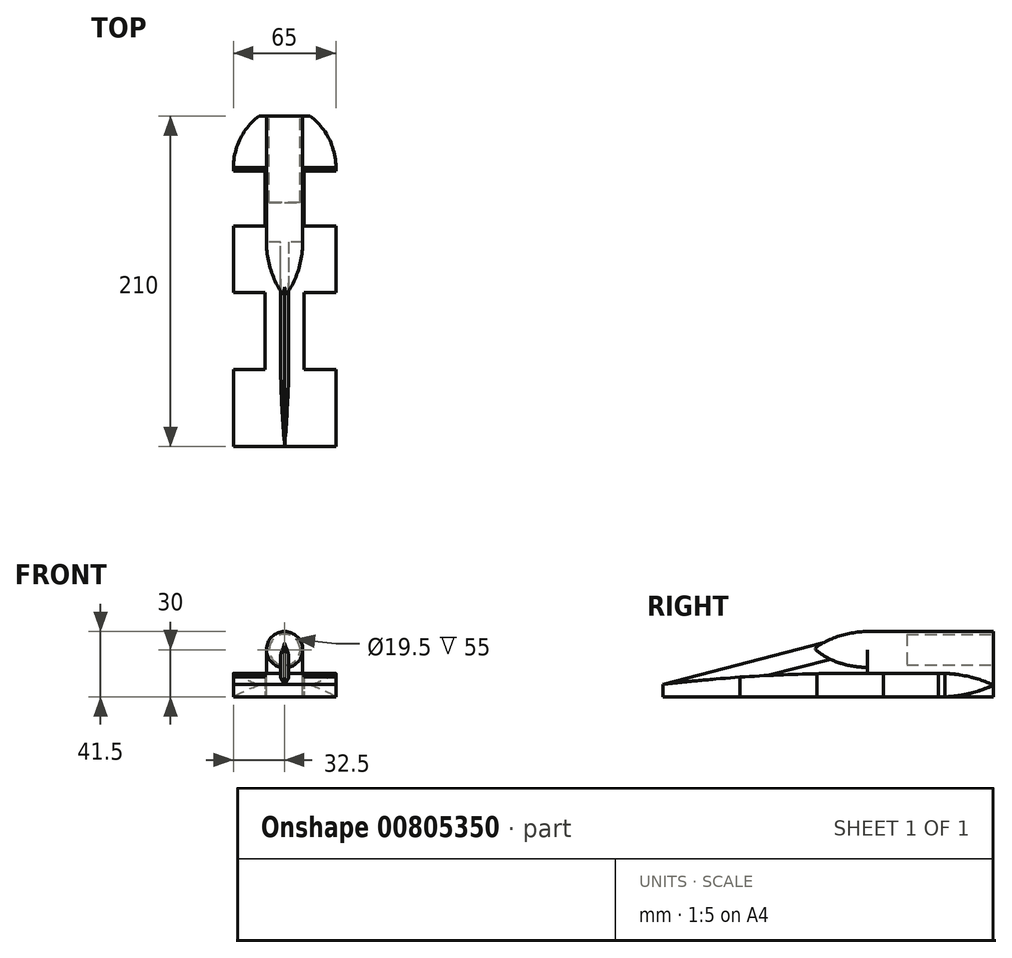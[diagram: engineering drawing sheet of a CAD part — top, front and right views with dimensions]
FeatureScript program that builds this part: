
annotation { "Feature Type Name" : "Feature", "Feature Type Description" : "" }
export const myFeature = defineFeature(function(context is Context, id is Id, definition is map)
    precondition{}
    {
        {
            var Q0;
            Q0=qCreatedBy(makeId("Right.planeOp"),FACE);
            var sketch = newSketch(context, id + "F0", { "sketchPlane" : qUnion([Q0])});
            skLineSegment(sketch, "E0", {"start": v(0, 0) * mm, "end": v(210, 0) * mm});
            skLineSegment(sketch, "E1", {"start": v(210, 0) * mm, "end": v(210, 15) * mm});
            skLineSegment(sketch, "E2", {"start": v(210, 15) * mm, "end": v(120, 15) * mm});
            skArc(sketch, "E3", {"start": v(120, 15) * mm, "mid": v(59.9, 13.25) * mm, "end": v(0, 8) * mm});
            skLineSegment(sketch, "E4", {"start": v(0, 8) * mm, "end": v(0, 0) * mm});
            skSolve(sketch);
        }
        {
            var Q0;
            Q0=makeQuery(id+"F0.imprint","IMPRINT",FACE,{"disambiguationData":[TD([[makeQuery(id+"F0.imprint","IMPRINT",EDGE,{"derivedFrom":sQuery(id+"F0.wireOp",EDGE,"E0")}),1.0]])]});
            extrude(context, id + "F1", {"entities" : qUnion([Q0]), "depth" : 32.5 * mm, "offsetDistance" : 25 * mm});
        }
        {
            var Q0;
            Q0=makeQuery(id+"F1.opExtrude","SWEPT_FACE",FACE,{"disambiguationData":[OSD([sQuery(id+"F0.wireOp",EDGE,"E0")])]});
            var sketch = newSketch(context, id + "F2", { "sketchPlane" : qUnion([Q0])});
            skLineSegment(sketch, "E5", {"start": v(32.5, -49) * mm, "end": v(12.5, -49) * mm});
            skLineSegment(sketch, "E6", {"start": v(12.5, -49) * mm, "end": v(12.5, -98) * mm});
            skLineSegment(sketch, "E7", {"start": v(12.5, -98) * mm, "end": v(32.5, -98) * mm});
            skLineSegment(sketch, "E8", {"start": v(32.5, -140) * mm, "end": v(12.5, -140) * mm});
            skLineSegment(sketch, "E9", {"start": v(12.5, -140) * mm, "end": v(12.5, -175) * mm});
            skLineSegment(sketch, "E10", {"start": v(12.5, -175) * mm, "end": v(32.5, -175) * mm});
            skArc(sketch, "E11", {"start": v(16.25, -210) * mm, "mid": v(28.72, -194.52) * mm, "end": v(32.5, -175) * mm});
            skSolve(sketch);
        }
        {
            var Q0;
            {var subQ0=sQuery(id+"F0.wireOp",EDGE,"E3");var subQ1=sQuery(id+"F0.wireOp",EDGE,"E2");var subQ2=sQuery(id+"F0.wireOp",EDGE,"E0");Q0=makeQuery(id+"F4.boolean.opBoolean","SPLIT",FACE,{"disambiguationData":[TD([makeQuery(id+"F4.opExtrude","SWEPT_FACE",FACE,{"disambiguationData":[OSD([sQuery(id+"F2.wireOp",EDGE,"E7")])]})])],"derivedFrom":makeQuery(id+"F1.opExtrude","CAP_FACE",FACE,{"disambiguationData":[OSD([subQ2,sQuery(id+"F0.wireOp",EDGE,"E1"),subQ1,subQ0,sQuery(id+"F0.wireOp",EDGE,"E4")])],"isStart":false})});}
            var sketch = newSketch(context, id + "F3", { "sketchPlane" : qUnion([Q0])});
            skLineSegment(sketch, "E12", {"start": v(175, 15) * mm, "end": v(175, 0) * mm});
            skArc(sketch, "E13", {"start": v(175, 0) * mm, "mid": v(192.92, 1.77) * mm, "end": v(210, 7.5) * mm});
            skArc(sketch, "E14", {"start": v(210, 7.5) * mm, "mid": v(192.92, 13.23) * mm, "end": v(175, 15) * mm});
            skSolve(sketch);
        }
        {
            var Q0;
            {var subQ0=sQuery(id+"F2.wireOp",EDGE,"E5");Q0=makeQuery(id+"F2.imprint","IMPRINT",FACE,{"disambiguationData":[TD([[makeQuery(id+"F2.imprint","IMPRINT",EDGE,{"derivedFrom":subQ0}),1.0]])]});}
            var Q1;
            {var subQ0=sQuery(id+"F2.wireOp",EDGE,"E8");Q1=makeQuery(id+"F2.imprint","IMPRINT",FACE,{"disambiguationData":[TD([[makeQuery(id+"F2.imprint","IMPRINT",EDGE,{"derivedFrom":subQ0}),1.0]])]});}
            var Q2;
            {var subQ0=sQuery(id+"F2.wireOp",EDGE,"E11");var subQ1=sQuery(id+"F0.wireOp",EDGE,"E0");var subQ4=makeQuery(id+"F1.opExtrude","CAP_EDGE",EDGE,{"disambiguationData":[OSD([subQ1])],"isStart":false});var subQ5=makeQuery(id+"F2.imprint","INTERSECT",VERTEX,{"derivedFrom":[subQ4,subQ0]});Q2=makeQuery(id+"F2.imprint","IMPRINT",FACE,{"disambiguationData":[TD([[makeQuery(id+"F2.imprint","IMPRINT",EDGE,{"disambiguationData":[TD([[subQ5,1.0]])],"derivedFrom":subQ0}),-1.0]])]});}
            extrude(context, id + "F4", {"entities" : qUnion([Q0, Q1, Q2]), "operationType" : NewBodyOperationType.REMOVE, "endBound" : BoundingType.THROUGH_ALL, "oppositeDirection" : true, "depth" : 25 * mm, "offsetDistance" : 25 * mm});
        }
        {
            var Q0;
            {var subQ1=makeQuery(id+"F1.opExtrude","CAP_EDGE",EDGE,{"disambiguationData":[OSD([sQuery(id+"F0.wireOp",EDGE,"E1")])],"isStart":false});var subQ3=makeQuery(id+"F1.opExtrude","CAP_EDGE",EDGE,{"disambiguationData":[OSD([sQuery(id+"F0.wireOp",EDGE,"E2")])],"isStart":false});var subQ5=makeQuery(id+"F3.imprint","INTERSECT",VERTEX,{"derivedFrom":[subQ1,subQ3]});Q0=makeQuery(id+"F3.imprint","IMPRINT",FACE,{"disambiguationData":[TD([[makeQuery(id+"F3.imprint","IMPRINT",EDGE,{"disambiguationData":[TD([[subQ5,-1.0]])],"derivedFrom":subQ3}),1.0]])]});}
            var Q1;
            {var subQ1=makeQuery(id+"F1.opExtrude","CAP_EDGE",EDGE,{"disambiguationData":[OSD([sQuery(id+"F0.wireOp",EDGE,"E1")])],"isStart":false});var subQ3=makeQuery(id+"F1.opExtrude","CAP_EDGE",EDGE,{"disambiguationData":[OSD([sQuery(id+"F0.wireOp",EDGE,"E0")])],"isStart":false});var subQ5=makeQuery(id+"F3.imprint","INTERSECT",VERTEX,{"derivedFrom":[subQ3,subQ1]});Q1=makeQuery(id+"F3.imprint","IMPRINT",FACE,{"disambiguationData":[TD([[makeQuery(id+"F3.imprint","IMPRINT",EDGE,{"disambiguationData":[TD([[subQ5,1.0]])],"derivedFrom":subQ3}),1.0]])]});}
            extrude(context, id + "F5", {"entities" : qUnion([Q0, Q1]), "operationType" : NewBodyOperationType.REMOVE, "oppositeDirection" : true, "depth" : 21 * mm, "offsetDistance" : 25 * mm});
        }
        {
            var Q0;
            Q0=makeQuery(id+"F1.opExtrude","SWEPT_BODY",BODY,{"disambiguationData":[OSD([sQuery(id+"F0.wireOp",EDGE,"E0"),sQuery(id+"F0.wireOp",EDGE,"E1"),sQuery(id+"F0.wireOp",EDGE,"E2"),sQuery(id+"F0.wireOp",EDGE,"E3"),sQuery(id+"F0.wireOp",EDGE,"E4")])]});
            var Q1;
            Q1=qCreatedBy(makeId("Right.planeOp"),FACE);
            mirror(context, id + "F6", {"operationType" : NewBodyOperationType.ADD, "entities" : qUnion([Q0]), "mirrorPlane" : qUnion([Q1])});
        }
        {
            var Q0;
            {var subQ0=makeQuery(id+"F1.opExtrude","SWEPT_FACE",FACE,{"disambiguationData":[OSD([sQuery(id+"F0.wireOp",EDGE,"E1")])]});Q0=makeQuery(id+"F6.boolean.opBoolean","MERGE",FACE,{"derivedFrom":[subQ0,makeQuery(id+"F6.opPattern","COPY",FACE,{"derivedFrom":subQ0,"instanceName":"1"})]});}
            var sketch = newSketch(context, id + "F7", { "sketchPlane" : qUnion([Q0])});
            skLineSegment(sketch, "E15", {"start": v(-11.5, 15) * mm, "end": v(-11.5, 30) * mm});
            skLineSegment(sketch, "E16", {"start": v(11.5, 15) * mm, "end": v(11.5, 30) * mm});
            skArc(sketch, "E17", {"start": v(11.5, 30) * mm, "mid": v(0, 41.5) * mm, "end": v(-11.5, 30) * mm});
            skCircle(sketch, "E18", {"center": v(0, 30) * mm, "radius": 9.75 * mm});
            skSolve(sketch);
        }
        {
            var Q0;
            Q0=makeQuery(id+"F7.imprint","IMPRINT",FACE,{"disambiguationData":[TD([[makeQuery(id+"F7.imprint","IMPRINT",EDGE,{"derivedFrom":sQuery(id+"F7.wireOp",EDGE,"E18")}),1.0]])]});
            var Q1;
            Q1=makeQuery(id+"F7.imprint","IMPRINT",FACE,{"disambiguationData":[TD([[makeQuery(id+"F7.imprint","IMPRINT",EDGE,{"derivedFrom":sQuery(id+"F7.wireOp",EDGE,"E15")}),-1.0]])]});
            extrude(context, id + "F8", {"entities" : qUnion([Q0, Q1]), "operationType" : NewBodyOperationType.ADD, "oppositeDirection" : true, "depth" : 80 * mm, "offsetDistance" : 25 * mm});
        }
        {
            var Q0;
            Q0=makeQuery(id+"F7.imprint","IMPRINT",FACE,{"disambiguationData":[TD([[makeQuery(id+"F7.imprint","IMPRINT",EDGE,{"derivedFrom":sQuery(id+"F7.wireOp",EDGE,"E18")}),1.0]])]});
            extrude(context, id + "F9", {"entities" : qUnion([Q0]), "operationType" : NewBodyOperationType.REMOVE, "oppositeDirection" : true, "depth" : 55 * mm, "offsetDistance" : 25 * mm});
        }
        {
            var Q0;
            Q0=qCreatedBy(makeId("Right.planeOp"),FACE);
            var sketch = newSketch(context, id + "F10", { "sketchPlane" : qUnion([Q0])});
            skLineSegment(sketch, "E19.0", {"start": v(130, 15) * mm, "end": v(130, 30) * mm});
            skLineSegment(sketch, "E20", {"start": v(130, 41.5) * mm, "end": v(210, 41.5) * mm});
            skLineSegment(sketch, "E21", {"start": v(130, 30) * mm, "end": v(95, 30) * mm});
            skArc(sketch, "E22", {"start": v(130, 41.5) * mm, "mid": v(111.58, 38.55) * mm, "end": v(95, 30) * mm});
            skLineSegment(sketch, "E23", {"start": v(130, 41.5) * mm, "end": v(130, 30) * mm});
            skSolve(sketch);
        }
        {
            var Q0;
            Q0 = qSketchRegion(id + "F10", true);
            var Q1;
            Q1=sQuery(id+"F10.wireOp",EDGE,"E21");
            revolve(context, id + "F11", {"surfaceOperationType" : NewSurfaceOperationType.NEW, "entities" : qUnion([Q0]), "axis" : qUnion([Q1]), "revolveType" : RevolveType.FULL});
        }
        {
            var Q0;
            Q0=makeQuery(id+"F8.opExtrude","CAP_FACE",FACE,{"disambiguationData":[OSD([sQuery(id+"F0.wireOp",EDGE,"E1"),sQuery(id+"F0.wireOp",EDGE,"E2"),sQuery(id+"F7.wireOp",EDGE,"E15"),sQuery(id+"F7.wireOp",EDGE,"E16"),sQuery(id+"F7.wireOp",EDGE,"E17")])],"isStart":false});
            var sketch = newSketch(context, id + "F12", { "sketchPlane" : qUnion([Q0])});
            skPoint(sketch, "E24.0", {"position": v(0, 15) * mm});
            skLineSegment(sketch, "E25.0", {"start": v(32.5, 15) * mm, "end": v(-32.5, 15) * mm});
            skArc(sketch, "E26", {"start": v(0, 41.5) * mm, "mid": v(-2.22, 35.96) * mm, "end": v(-2.5, 30) * mm});
            skArc(sketch, "E27", {"start": v(2.5, 30) * mm, "mid": v(2.22, 35.96) * mm, "end": v(0, 41.5) * mm});
            skLineSegment(sketch, "E28", {"start": v(2.5, 30) * mm, "end": v(2.5, 15) * mm});
            skLineSegment(sketch, "E29", {"start": v(-2.5, 30) * mm, "end": v(-2.5, 15) * mm});
            skLineSegment(sketch, "E30", {"start": v(-2.5, 15) * mm, "end": v(2.5, 15) * mm});
            skSolve(sketch);
        }
        {
            var Q0;
            Q0=qCreatedBy(makeId("Right.planeOp"),FACE);
            var sketch = newSketch(context, id + "F13", { "sketchPlane" : qUnion([Q0])});
            skPoint(sketch, "E31.0", {"position": v(130, 41.5) * mm});
            skPoint(sketch, "E32.0", {"position": v(0, 8) * mm});
            skLineSegment(sketch, "E33", {"start": v(130, 41.5) * mm, "end": v(0, 8) * mm});
            skSolve(sketch);
        }
        {
            var Q0;
            Q0=makeQuery(id+"F12.imprint","IMPRINT",FACE,{"disambiguationData":[TD([[makeQuery(id+"F12.imprint","IMPRINT",EDGE,{"derivedFrom":sQuery(id+"F12.wireOp",EDGE,"E26")}),1.0]])]});
            var Q1;
            Q1=sQuery(id+"F13.wireOp",EDGE,"E33");
            sweep(context, id + "F14", {"operationType" : NewBodyOperationType.ADD, "profiles" : qUnion([Q0]), "path" : qUnion([Q1])});
        }
        {
            var Q0;
            {var subQ1=sQuery(id+"F13.wireOp",EDGE,"E33");var subQ3=makeQuery(id+"F1.opExtrude","SWEPT_FACE",FACE,{"disambiguationData":[OSD([sQuery(id+"F0.wireOp",EDGE,"E0")])]});var subQ4=sQuery(id+"F12.wireOp",EDGE,"E28");Q0=makeQuery(id+"F14.boolean.opBoolean","SPLIT",FACE,{"disambiguationData":[TD([subQ3])],"derivedFrom":makeQuery(id+"F14.opSweep","SWEPT_FACE",FACE,{"disambiguationData":[OSD([subQ4,subQ1])]})});}
            var sketch = newSketch(context, id + "F15", { "sketchPlane" : qUnion([Q0])});
            skLineSegment(sketch, "E34.0", {"start": v(0, -3.5) * mm, "end": v(0, 0) * mm});
            skLineSegment(sketch, "E35.0", {"start": v(0, -18.5) * mm, "end": v(0, -3.5) * mm});
            skLineSegment(sketch, "E36.0", {"start": v(71.8, 0) * mm, "end": v(0, -18.5) * mm});
            skLineSegment(sketch, "E37.0", {"start": v(0, 0) * mm, "end": v(49, 0) * mm});
            skLineSegment(sketch, "E38.0", {"start": v(49, 0) * mm, "end": v(98, 0) * mm});
            skFitSpline(sketch, "E39.0.0", {"points": [v(13.58, 0) * mm, v(9.05, 0) * mm, v(4.53, 0) * mm, v(0, 0) * mm]});
            skLineSegment(sketch, "E39.0.1", {"start": v(0, 0) * mm, "end": v(0, -3.5) * mm});
            skLineSegment(sketch, "E39.0.2", {"start": v(0, -3.5) * mm, "end": v(13.58, 0) * mm});
            skSolve(sketch);
        }
        {
            var Q0;
            Q0=makeQuery(id+"F15.imprint","IMPRINT",FACE,{"disambiguationData":[TD([[makeQuery(id+"F15.imprint","IMPRINT",EDGE,{"derivedFrom":sQuery(id+"F15.wireOp",EDGE,"E39.0.0")}),1.0]])]});
            var Q1;
            Q1=makeQuery(id+"F15.imprint","IMPRINT",FACE,{"disambiguationData":[TD([[makeQuery(id+"F15.imprint","IMPRINT",EDGE,{"derivedFrom":sQuery(id+"F15.wireOp",EDGE,"E35.0")}),-1.0]])]});
            extrude(context, id + "F16", {"entities" : qUnion([Q0, Q1]), "operationType" : NewBodyOperationType.REMOVE, "endBound" : BoundingType.THROUGH_ALL, "oppositeDirection" : true, "depth" : 25 * mm, "offsetDistance" : 25 * mm});
        }
        {
            var Q0;
            {var subQ0=sQuery(id+"F0.wireOp",EDGE,"E0");var subQ1=sQuery(id+"F0.wireOp",EDGE,"E3");var subQ2=sQuery(id+"F0.wireOp",EDGE,"E4");Q0=makeQuery(id+"F4.boolean.opBoolean","SPLIT",FACE,{"disambiguationData":[TD([makeQuery(id+"F1.opExtrude","SWEPT_FACE",FACE,{"disambiguationData":[OSD([subQ2])]})])],"derivedFrom":makeQuery(id+"F1.opExtrude","CAP_FACE",FACE,{"disambiguationData":[OSD([subQ0,sQuery(id+"F0.wireOp",EDGE,"E1"),sQuery(id+"F0.wireOp",EDGE,"E2"),subQ1,subQ2])],"isStart":false})});}
            var sketch = newSketch(context, id + "F17", { "sketchPlane" : qUnion([Q0])});
            skLineSegment(sketch, "E40.0", {"start": v(13.58, 0) * mm, "end": v(0, -3.5) * mm});
            skLineSegment(sketch, "E41.0", {"start": v(0, -3.5) * mm, "end": v(0, 0) * mm});
            skLineSegment(sketch, "E42", {"start": v(13.58, 0) * mm, "end": v(0, 0) * mm});
            skSolve(sketch);
        }
        {
            var Q0;
            Q0=makeQuery(id+"F17.imprint","IMPRINT",FACE,{"disambiguationData":[TD([[makeQuery(id+"F17.imprint","IMPRINT",EDGE,{"derivedFrom":sQuery(id+"F17.wireOp",EDGE,"E40.0")}),-1.0]])]});
            extrude(context, id + "F18", {"entities" : qUnion([Q0]), "operationType" : NewBodyOperationType.REMOVE, "endBound" : BoundingType.THROUGH_ALL, "oppositeDirection" : true, "depth" : 25 * mm, "offsetDistance" : 25 * mm});
        }
    });
